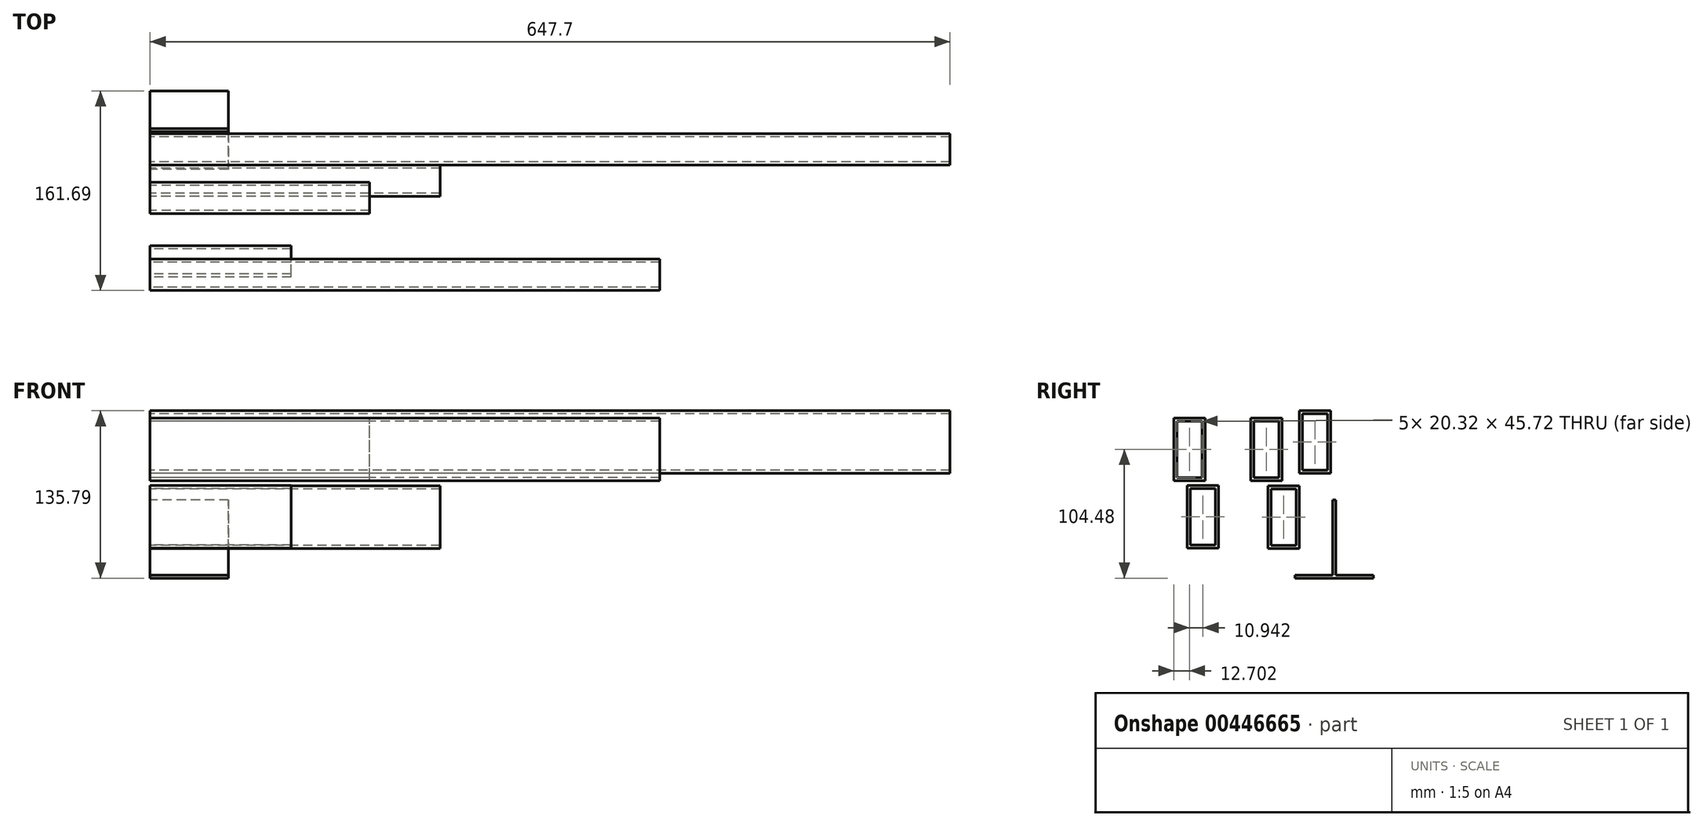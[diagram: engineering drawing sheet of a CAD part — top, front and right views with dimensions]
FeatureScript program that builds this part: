
annotation { "Feature Type Name" : "Feature", "Feature Type Description" : "" }
export const myFeature = defineFeature(function(context is Context, id is Id, definition is map)
    precondition{}
    {
        {
            var Q0;
            Q0=qCreatedBy(makeId("Right.planeOp"),FACE);
            var sketch = newSketch(context, id + "F0", { "sketchPlane" : qUnion([Q0])});
            skLineSegment(sketch, "E0.bottom", {"start": v(0, 0) * mm, "end": v(25.4, 0) * mm});
            skLineSegment(sketch, "E0.top", {"start": v(0, 50.8) * mm, "end": v(25.4, 50.8) * mm});
            skLineSegment(sketch, "E0.left", {"start": v(0, 0) * mm, "end": v(0, 50.8) * mm});
            skLineSegment(sketch, "E0.right", {"start": v(25.4, 0) * mm, "end": v(25.4, 50.8) * mm});
            skLineSegment(sketch, "E1.0", {"start": v(2.54, 48.26) * mm, "end": v(22.86, 48.26) * mm});
            skLineSegment(sketch, "E1.1", {"start": v(2.54, 2.54) * mm, "end": v(2.54, 48.26) * mm});
            skLineSegment(sketch, "E1.2", {"start": v(2.54, 2.54) * mm, "end": v(22.86, 2.54) * mm});
            skLineSegment(sketch, "E1.3", {"start": v(22.86, 2.54) * mm, "end": v(22.86, 48.26) * mm});
            skSolve(sketch);
        }
        {
            var Q0;
            Q0=makeQuery(id+"F0.imprint","IMPRINT",FACE,{"disambiguationData":[TD([[makeQuery(id+"F0.imprint","IMPRINT",EDGE,{"derivedFrom":sQuery(id+"F0.wireOp",EDGE,"E0.bottom")}),1.0]])]});
            extrude(context, id + "F1", {"entities" : qUnion([Q0]), "depth" : 177.8 * mm, "offsetDistance" : 25.4 * mm});
        }
        {
            var Q0;
            Q0=qCreatedBy(makeId("Right.planeOp"),FACE);
            var sketch = newSketch(context, id + "F2", { "sketchPlane" : qUnion([Q0])});
            skLineSegment(sketch, "E2.bottom", {"start": v(-62.38, 0) * mm, "end": v(-36.98, 0) * mm});
            skLineSegment(sketch, "E2.top", {"start": v(-62.38, 50.8) * mm, "end": v(-36.98, 50.8) * mm});
            skLineSegment(sketch, "E2.left", {"start": v(-62.38, 0) * mm, "end": v(-62.38, 50.8) * mm});
            skLineSegment(sketch, "E2.right", {"start": v(-36.98, 0) * mm, "end": v(-36.98, 50.8) * mm});
            skLineSegment(sketch, "E3.0", {"start": v(-59.84, 48.26) * mm, "end": v(-39.52, 48.26) * mm});
            skLineSegment(sketch, "E3.1", {"start": v(-59.84, 2.54) * mm, "end": v(-59.84, 48.26) * mm});
            skLineSegment(sketch, "E3.2", {"start": v(-59.84, 2.54) * mm, "end": v(-39.52, 2.54) * mm});
            skLineSegment(sketch, "E3.3", {"start": v(-39.52, 2.54) * mm, "end": v(-39.52, 48.26) * mm});
            skSolve(sketch);
        }
        {
            var Q0;
            Q0 = qSketchRegion(id + "F2", true);
            extrude(context, id + "F3", {"entities" : qUnion([Q0]), "depth" : 412.75 * mm, "offsetDistance" : 25.4 * mm});
        }
        {
            var Q0;
            Q0=qCreatedBy(makeId("Right.planeOp"),FACE);
            var sketch = newSketch(context, id + "F4", { "sketchPlane" : qUnion([Q0])});
            skLineSegment(sketch, "E4.bottom", {"start": v(-51.44, -54.77) * mm, "end": v(-26.04, -54.77) * mm});
            skLineSegment(sketch, "E4.top", {"start": v(-51.44, -3.97) * mm, "end": v(-26.04, -3.97) * mm});
            skLineSegment(sketch, "E4.left", {"start": v(-51.44, -54.77) * mm, "end": v(-51.44, -3.97) * mm});
            skLineSegment(sketch, "E4.right", {"start": v(-26.04, -54.77) * mm, "end": v(-26.04, -3.97) * mm});
            skLineSegment(sketch, "E5.0", {"start": v(-48.9, -6.51) * mm, "end": v(-28.58, -6.51) * mm});
            skLineSegment(sketch, "E5.1", {"start": v(-48.9, -52.23) * mm, "end": v(-48.9, -6.51) * mm});
            skLineSegment(sketch, "E5.2", {"start": v(-48.9, -52.23) * mm, "end": v(-28.58, -52.23) * mm});
            skLineSegment(sketch, "E5.3", {"start": v(-28.58, -52.23) * mm, "end": v(-28.58, -6.51) * mm});
            skSolve(sketch);
        }
        {
            var Q0;
            Q0 = qSketchRegion(id + "F4", true);
            extrude(context, id + "F5", {"entities" : qUnion([Q0]), "depth" : 114.3 * mm, "offsetDistance" : 25.4 * mm});
        }
        {
            var Q0;
            Q0=qCreatedBy(makeId("Right.planeOp"),FACE);
            var sketch = newSketch(context, id + "F6", { "sketchPlane" : qUnion([Q0])});
            skLineSegment(sketch, "E6.bottom", {"start": v(13.86, -54.92) * mm, "end": v(39.26, -54.92) * mm});
            skLineSegment(sketch, "E6.top", {"start": v(13.86, -4.12) * mm, "end": v(39.26, -4.12) * mm});
            skLineSegment(sketch, "E6.left", {"start": v(13.86, -54.92) * mm, "end": v(13.86, -4.12) * mm});
            skLineSegment(sketch, "E6.right", {"start": v(39.26, -54.92) * mm, "end": v(39.26, -4.12) * mm});
            skLineSegment(sketch, "E7.0", {"start": v(16.4, -6.66) * mm, "end": v(36.72, -6.66) * mm});
            skLineSegment(sketch, "E7.1", {"start": v(16.4, -52.38) * mm, "end": v(16.4, -6.66) * mm});
            skLineSegment(sketch, "E7.2", {"start": v(16.4, -52.38) * mm, "end": v(36.72, -52.38) * mm});
            skLineSegment(sketch, "E7.3", {"start": v(36.72, -52.38) * mm, "end": v(36.72, -6.66) * mm});
            skSolve(sketch);
        }
        {
            var Q0;
            Q0=makeQuery(id+"F6.imprint","IMPRINT",FACE,{"disambiguationData":[TD([[makeQuery(id+"F6.imprint","IMPRINT",EDGE,{"derivedFrom":sQuery(id+"F6.wireOp",EDGE,"E6.bottom")}),1.0]])]});
            extrude(context, id + "F7", {"entities" : qUnion([Q0]), "depth" : 234.95 * mm, "offsetDistance" : 25.4 * mm});
        }
        {
            var Q0;
            Q0=qCreatedBy(makeId("Right.planeOp"),FACE);
            var sketch = newSketch(context, id + "F8", { "sketchPlane" : qUnion([Q0])});
            skLineSegment(sketch, "E8.bottom", {"start": v(39.16, 5.9) * mm, "end": v(64.56, 5.9) * mm});
            skLineSegment(sketch, "E8.top", {"start": v(39.16, 56.7) * mm, "end": v(64.56, 56.7) * mm});
            skLineSegment(sketch, "E8.left", {"start": v(39.16, 5.9) * mm, "end": v(39.16, 56.7) * mm});
            skLineSegment(sketch, "E8.right", {"start": v(64.56, 5.9) * mm, "end": v(64.56, 56.7) * mm});
            skLineSegment(sketch, "E9.0", {"start": v(41.7, 54.17) * mm, "end": v(62.02, 54.17) * mm});
            skLineSegment(sketch, "E9.1", {"start": v(41.7, 8.45) * mm, "end": v(41.7, 54.17) * mm});
            skLineSegment(sketch, "E9.2", {"start": v(41.7, 8.45) * mm, "end": v(62.02, 8.45) * mm});
            skLineSegment(sketch, "E9.3", {"start": v(62.02, 8.45) * mm, "end": v(62.02, 54.17) * mm});
            skSolve(sketch);
        }
        {
            var Q0;
            Q0=makeQuery(id+"F8.imprint","IMPRINT",FACE,{"disambiguationData":[TD([[makeQuery(id+"F8.imprint","IMPRINT",EDGE,{"derivedFrom":sQuery(id+"F8.wireOp",EDGE,"E8.bottom")}),1.0]])]});
            extrude(context, id + "F9", {"entities" : qUnion([Q0]), "depth" : 647.7 * mm, "offsetDistance" : 25.4 * mm});
        }
        {
            var Q0;
            Q0=qCreatedBy(makeId("Right.planeOp"),FACE);
            var sketch = newSketch(context, id + "F10", { "sketchPlane" : qUnion([Q0])});
            skLineSegment(sketch, "E10", {"start": v(35.8, -76.54) * mm, "end": v(66.29, -76.54) * mm});
            skLineSegment(sketch, "E11", {"start": v(66.29, -76.54) * mm, "end": v(66.29, -15.58) * mm});
            skLineSegment(sketch, "E12", {"start": v(66.29, -15.58) * mm, "end": v(68.83, -15.58) * mm});
            skLineSegment(sketch, "E13", {"start": v(68.83, -15.58) * mm, "end": v(68.83, -76.54) * mm});
            skLineSegment(sketch, "E14", {"start": v(68.83, -76.54) * mm, "end": v(99.3, -76.54) * mm});
            skLineSegment(sketch, "E15", {"start": v(99.3, -76.54) * mm, "end": v(99.3, -79.08) * mm});
            skLineSegment(sketch, "E16", {"start": v(99.3, -79.08) * mm, "end": v(35.8, -79.08) * mm});
            skLineSegment(sketch, "E17", {"start": v(35.8, -76.54) * mm, "end": v(35.8, -79.08) * mm});
            skSolve(sketch);
        }
        {
            var Q0;
            Q0 = qSketchRegion(id + "F10", true);
            extrude(context, id + "F11", {"entities" : qUnion([Q0]), "depth" : 63.5 * mm, "offsetDistance" : 25.4 * mm});
        }
    });
